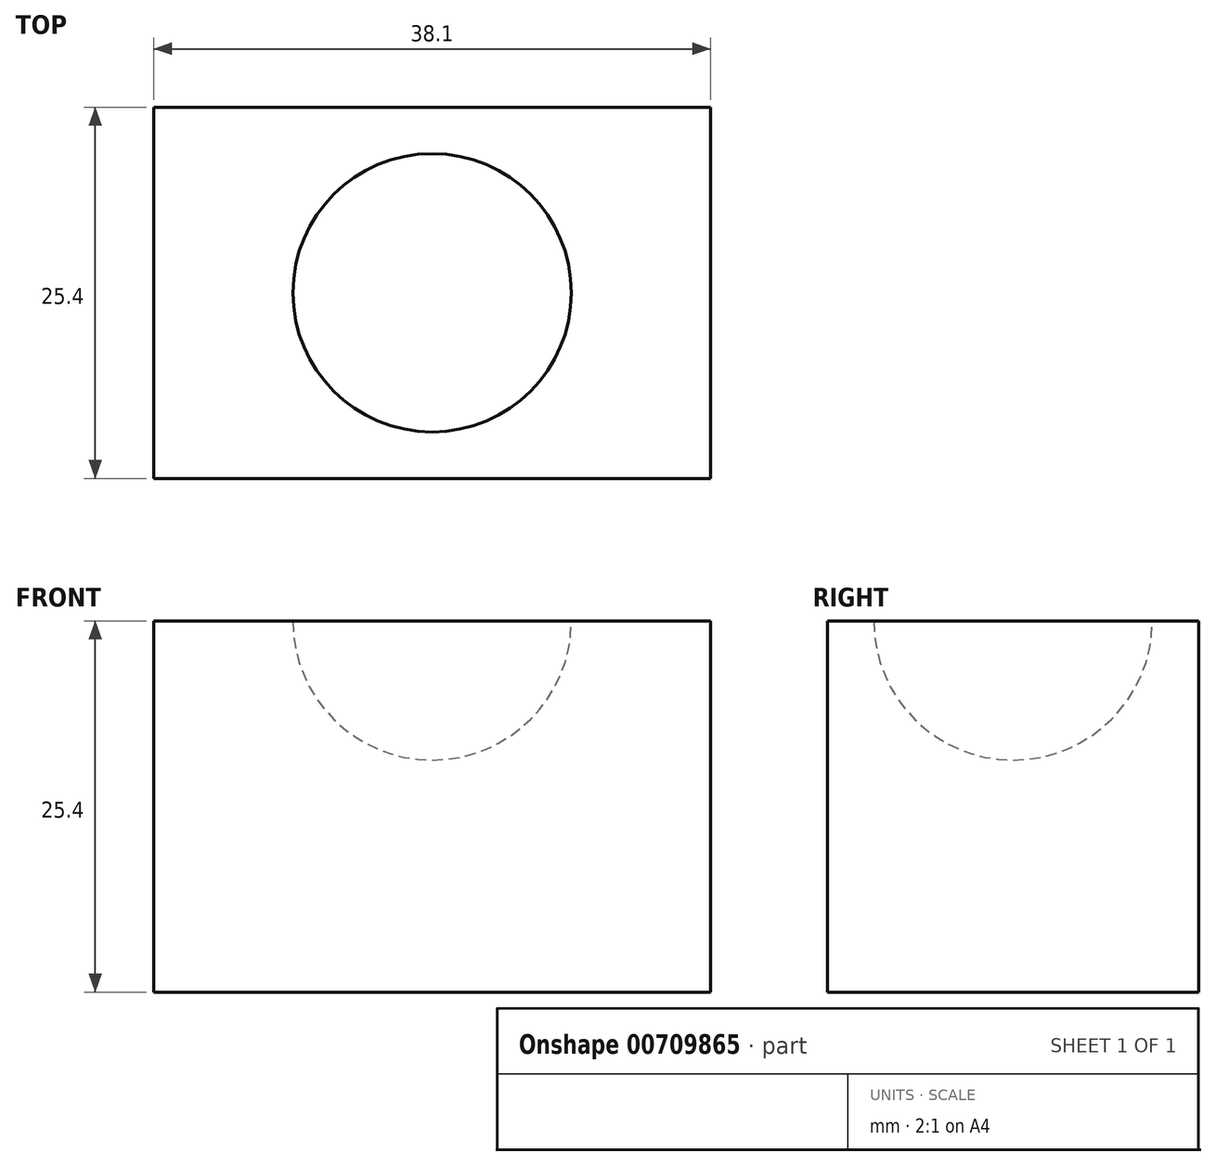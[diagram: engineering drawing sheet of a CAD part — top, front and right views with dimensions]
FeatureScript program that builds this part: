
annotation { "Feature Type Name" : "Feature", "Feature Type Description" : "" }
export const myFeature = defineFeature(function(context is Context, id is Id, definition is map)
    precondition{}
    {
        {
            var Q0;
            Q0=qCreatedBy(makeId("Top.planeOp"),FACE);
            var sketch = newSketch(context, id + "F0", { "sketchPlane" : qUnion([Q0])});
            skLineSegment(sketch, "E0.bottom", {"start": v(-19.05, 12.7) * mm, "end": v(19.05, 12.7) * mm});
            skLineSegment(sketch, "E0.top", {"start": v(-19.05, -12.7) * mm, "end": v(19.05, -12.7) * mm});
            skLineSegment(sketch, "E0.left", {"start": v(-19.05, 12.7) * mm, "end": v(-19.05, -12.7) * mm});
            skLineSegment(sketch, "E0.right", {"start": v(19.05, 12.7) * mm, "end": v(19.05, -12.7) * mm});
            skSolve(sketch);
        }
        {
            var Q0;
            Q0=makeQuery(id+"F0.imprint","IMPRINT",FACE,{"disambiguationData":[TD([[makeQuery(id+"F0.imprint","IMPRINT",EDGE,{"derivedFrom":sQuery(id+"F0.wireOp",EDGE,"E0.bottom")}),-1.0]])]});
            extrude(context, id + "F1", {"entities" : qUnion([Q0]), "depth" : 25.4 * mm, "offsetDistance" : 25.4 * mm});
        }
        {
            var Q0;
            Q0=makeQuery(id+"F1.opExtrude","CAP_FACE",FACE,{"disambiguationData":[OSD([sQuery(id+"F0.wireOp",EDGE,"E0.bottom"),sQuery(id+"F0.wireOp",EDGE,"E0.top"),sQuery(id+"F0.wireOp",EDGE,"E0.left"),sQuery(id+"F0.wireOp",EDGE,"E0.right")])],"isStart":false});
            var sketch = newSketch(context, id + "F2", { "sketchPlane" : qUnion([Q0])});
            skLineSegment(sketch, "E1", {"start": v(0, 9.53) * mm, "end": v(0, -9.53) * mm});
            skPoint(sketch, "E1.startSnap0", {"position": v(0, 12.7) * mm});
            skArc(sketch, "E2", {"start": v(0, -9.53) * mm, "mid": v(9.53, 0) * mm, "end": v(0, 9.53) * mm});
            skSolve(sketch);
        }
        {
            var Q0;
            Q0 = qSketchRegion(id + "F2", true);
            var Q1;
            Q1=sQuery(id+"F2.wireOp",EDGE,"E1");
            revolve(context, id + "F3", {"operationType" : NewBodyOperationType.REMOVE, "surfaceOperationType" : NewSurfaceOperationType.NEW, "entities" : qUnion([Q0]), "axis" : qUnion([Q1]), "revolveType" : RevolveType.FULL, "oppositeDirection" : true});
        }
    });
